# Revit family: LBV235_99
name_source: partatom
category: Structural Connections
revit_build: Autodesk Revit 2014 (Build: 20130308_1515(x64)
units: mm (PartAtom-declared; Revit-internal decimal feet)

## types (1)
- LBV235_99
    A = 99 mm  [stored 0.324803 ft]
    B = 235 mm  [stored 0.770997 ft]
    C = 64 mm  [stored 0.209974 ft]
    D = 64 mm  [stored 0.209974 ft]
    Date Last Modified = September 09, 2016
    Default Elevation = 0 mm  [stored 0 ft]
    Description = Top Flange Joist Hanger
    E = 64 mm  [stored 0.209974 ft]
    F = 66 mm
    Family Version = 1.0.0
    Manufacturer = Simpson Strong-Tie Company Inc.
    Model = LBV235/99
    Model Disclaimer = Contact Simpson Strong-Tie Company Inc. for more information
    Product Type = Top Flange Joist Hanger
    Provide Feedback = http://www.strongtie.com
    URL = www.strongtie.eu\s\LBV
    t = 2 mm  [stored 0.00656168 ft]

note: [stored X ft] marks values corroborated as IEEE doubles in the binary element streams (Revit-internal decimal feet)

## geometry (parser evidence)
native form markers: Blend x77, Sweep x1
no freeform markers — native parametric forms only
